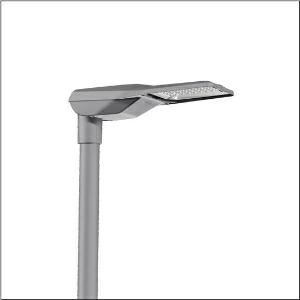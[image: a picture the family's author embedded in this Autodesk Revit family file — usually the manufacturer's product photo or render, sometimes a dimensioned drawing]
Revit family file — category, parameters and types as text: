
# Revit family: streetlight_sl_21_iq_mini___st1_0a_5xe2d41d08gb_4d7e
name_source: partatom
category: Lighting Fixtures
units: mm (PartAtom-declared; Revit-internal decimal feet)

## family parameters
Cut with Voids When Loaded = No
Host = Face
Light Source = No
Part Type = Normal
Room Calculation Point = No
Round Connector Dimension = Use Diameter
Shared = No

## types (1)
- --- (1 x LED, 5920 lm, 37.1 W, 4000K)
    Apparent Load = 37 VA
    CIE Flux Codes = 37 72 97 100 100
    Color Rendering = 70
    Color Temperature = 4000K
    Default Elevation = 1800 mm
    Description = Streetlight SL 21 iQ mini, mast luminaire, primary light control with lens, of PMMA, primary optical cover: cover, of toughened safety glass, transparent, light distribution: ST1.0a, light emission: direct distribution, primary light characteristic: asymmetric, installation type: post-top, side-entry, LED, High Power LED, rated luminous flux: 5.920lm, luminous efficacy: 160lm/W, light colour: 740, colour temperature: 4000K, control gear: iQ-Comfort, control: Auto-Match, Temp-Guard, Lumen-Switch, Night-Set, Smart-Wire, Light-Fading, Desk-Remote (wireless, voltage-free reading and setting of iQ features in the workshop via application-optimized NFC function/RFID function), optimised constant luminous flux control (CLO 2.0), pre-setting: linear dimming characteristic, mains connection: 220..240V, AC, 50/60Hz, start of lifetime: 37W, end of service life: 39W, reduction: 18W, luminaire housing, of diecast aluminium, powder-coated, SITECO metallic grey (DB 702S), corrosivity category C5 high according to DIN EN ISO 12944, please order mast flange separately, inclination adjustable: 0°, 5°, 10°, 15°, sealing non-destructively replaceable, multi-level sealing system, length: 628mm, width: 235mm, height: 110mm, mast flange for spigot size: 42mm (side-entry): 5XC10008XM4, 60/48mm (side-entry/post-top): 5XC10108XM2, 76/60mm (side-entry/post-top): 5XC10108XM1, mounting height: 4..8m, protection rating (complete): IP66, insulation class (complete): insulation class II (safety insulation), certification: CE, ENEC, ENEC+, VDE, impact resistance: IK10, permissible operating ambient temperature for outdoor applications: -40..+50°C, standard-compliant lighting for roads and squares, packaging unit: 1 piece

Light Distribution: ST1.0a
    Height = 110 mm
    Lamp = 1 x LED
    Lamp Light Flux = 5920 lm
    Lamp Power = 37.1 W
    Lamp count = 1
    Length = 625 mm
    Luminous efficacy = 160 lm/W
    Manufacturer = Siteco
    ModVariant = No
    Model = 5XE2D41D08GB
    Mounting Place = Pole
    Mounting Type = Pole top
    Number of Poles = 1
    OnlyDefault = Yes
    Power Factor = 1
    Product Name = Streetlight SL 21 iQ mini | ST1.0a
    Product group = mast luminaire | pylon top
    ProductGroupID = 6100
    Protection Class = Protection class II
    Protection Degree = IP 66
    RLX_Detail_Level = 1
    RLX_Emergency_Light_Flux = 0 lm
    RLX_Emergency_Type = 0
    RLX_Emergency_Type_DB = No
    RlxData = <blob elided: 26317 chars, md5=cbfa02b1>
    Socket = socket
    Standby Power = 0 W
    System Light Flux = 5920 lm
    System Power = 37 W
    Type Comments = factory setting: luminous flux: 100 % | dim-lin: 254 | 385 mA
    Type Image = l_1003519.jpg
    URL = http://relux.com
    VarID = @adj_187899
    Voltage = 0 V
    Weight = 0.00 kg
    Width = 234 mm

## geometry (parser evidence)
native form markers: Blend x4, Sweep x13
no freeform markers — native parametric forms only
